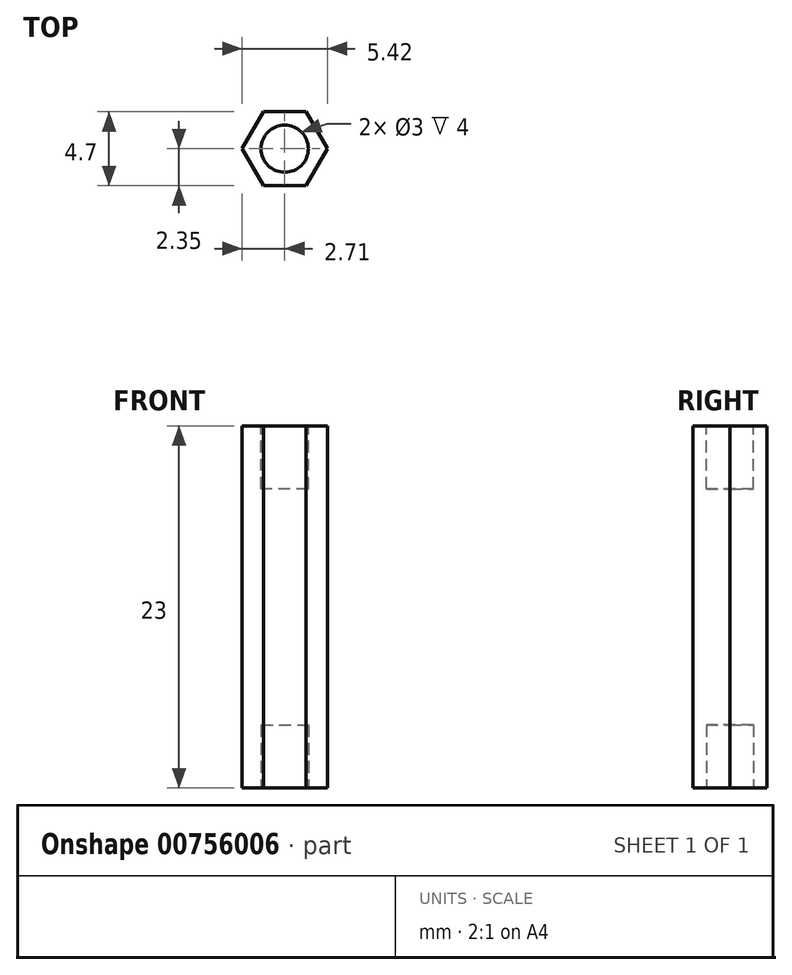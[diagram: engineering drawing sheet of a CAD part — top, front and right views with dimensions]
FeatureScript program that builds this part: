
annotation { "Feature Type Name" : "Feature", "Feature Type Description" : "" }
export const myFeature = defineFeature(function(context is Context, id is Id, definition is map)
    precondition{}
    {
        {
            var Q0;
            Q0=qCreatedBy(makeId("Top.planeOp"),FACE);
            var sketch = newSketch(context, id + "F0", { "sketchPlane" : qUnion([Q0])});
            skCircle(sketch, "E0.cCircle", {"center": v(0, 0) * mm, "radius": 2.35 * mm, "construction": true});
            skLineSegment(sketch, "E0.0", {"start": v(1.36, -2.35) * mm, "end": v(-1.36, -2.35) * mm});
            skLineSegment(sketch, "E0.1", {"start": v(-1.36, -2.35) * mm, "end": v(-2.71, 0) * mm});
            skLineSegment(sketch, "E0.2", {"start": v(-2.71, 0) * mm, "end": v(-1.36, 2.35) * mm});
            skLineSegment(sketch, "E0.3", {"start": v(-1.36, 2.35) * mm, "end": v(1.36, 2.35) * mm});
            skLineSegment(sketch, "E0.4", {"start": v(1.36, 2.35) * mm, "end": v(2.71, 0) * mm});
            skLineSegment(sketch, "E0.5", {"start": v(2.71, 0) * mm, "end": v(1.36, -2.35) * mm});
            skPoint(sketch, "E0.0.midPoint", {"position": v(0, -2.35) * mm});
            skSolve(sketch);
        }
        {
            var Q0;
            Q0=makeQuery(id+"F0.imprint","IMPRINT",FACE,{"disambiguationData":[TD([[makeQuery(id+"F0.imprint","IMPRINT",EDGE,{"derivedFrom":sQuery(id+"F0.wireOp",EDGE,"E0.0")}),-1.0]])]});
            extrude(context, id + "F1", {"entities" : qUnion([Q0]), "depth" : 23 * mm, "offsetDistance" : 25 * mm});
        }
        {
            var Q0;
            Q0=makeQuery(id+"F1.opExtrude","CAP_FACE",FACE,{"disambiguationData":[OSD([sQuery(id+"F0.wireOp",EDGE,"E0.0"),sQuery(id+"F0.wireOp",EDGE,"E0.1"),sQuery(id+"F0.wireOp",EDGE,"E0.2"),sQuery(id+"F0.wireOp",EDGE,"E0.3"),sQuery(id+"F0.wireOp",EDGE,"E0.4"),sQuery(id+"F0.wireOp",EDGE,"E0.5")])],"isStart":false});
            var sketch = newSketch(context, id + "F2", { "sketchPlane" : qUnion([Q0])});
            skCircle(sketch, "E1", {"center": v(0, 0) * mm, "radius": 1.5 * mm});
            skSolve(sketch);
        }
        {
            var Q0;
            Q0=makeQuery(id+"F2.imprint","IMPRINT",FACE,{"disambiguationData":[TD([[makeQuery(id+"F2.imprint","IMPRINT",EDGE,{"derivedFrom":sQuery(id+"F2.wireOp",EDGE,"E1")}),1.0]])]});
            extrude(context, id + "F3", {"entities" : qUnion([Q0]), "operationType" : NewBodyOperationType.REMOVE, "oppositeDirection" : true, "depth" : 4 * mm, "offsetDistance" : 25 * mm});
        }
        {
            var Q0;
            Q0=makeQuery(id+"F1.opExtrude","CAP_FACE",FACE,{"disambiguationData":[OSD([sQuery(id+"F0.wireOp",EDGE,"E0.0"),sQuery(id+"F0.wireOp",EDGE,"E0.1"),sQuery(id+"F0.wireOp",EDGE,"E0.2"),sQuery(id+"F0.wireOp",EDGE,"E0.3"),sQuery(id+"F0.wireOp",EDGE,"E0.4"),sQuery(id+"F0.wireOp",EDGE,"E0.5")])],"isStart":true});
            var sketch = newSketch(context, id + "F4", { "sketchPlane" : qUnion([Q0])});
            skCircle(sketch, "E2", {"center": v(0, 0) * mm, "radius": 1.5 * mm});
            skSolve(sketch);
        }
        {
            var Q0;
            Q0=makeQuery(id+"F4.imprint","IMPRINT",FACE,{"disambiguationData":[TD([[makeQuery(id+"F4.imprint","IMPRINT",EDGE,{"derivedFrom":sQuery(id+"F4.wireOp",EDGE,"E2")}),1.0]])]});
            extrude(context, id + "F5", {"entities" : qUnion([Q0]), "operationType" : NewBodyOperationType.REMOVE, "oppositeDirection" : true, "depth" : 4 * mm, "offsetDistance" : 25 * mm});
        }
    });
